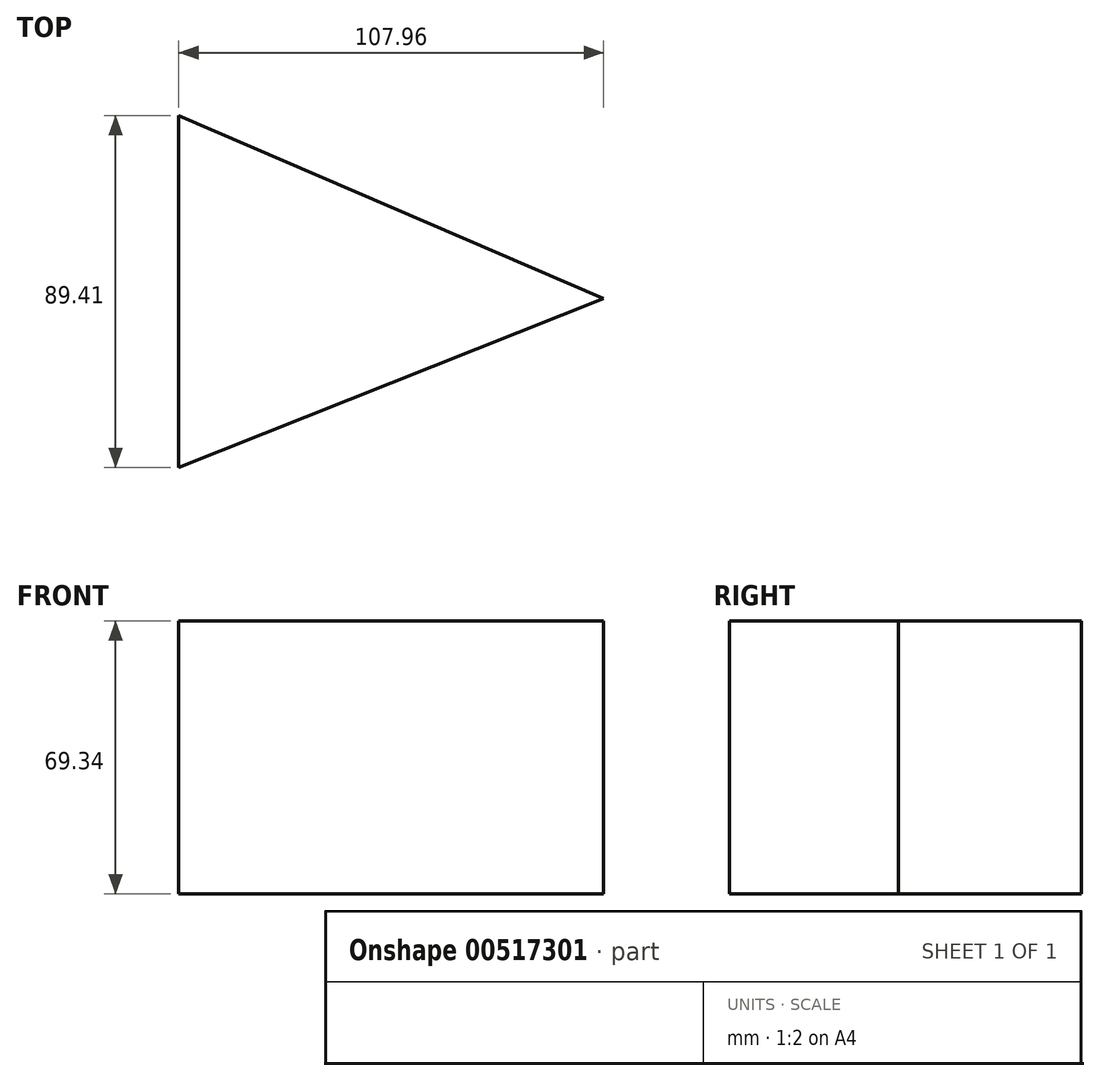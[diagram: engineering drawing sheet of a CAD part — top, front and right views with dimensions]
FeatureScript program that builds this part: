
annotation { "Feature Type Name" : "Feature", "Feature Type Description" : "" }
export const myFeature = defineFeature(function(context is Context, id is Id, definition is map)
    precondition{}
    {
        {
            var Q0;
            Q0=qCreatedBy(makeId("Top.planeOp"),FACE);
            var sketch = newSketch(context, id + "F0", { "sketchPlane" : qUnion([Q0])});
            skLineSegment(sketch, "E0.bottom", {"start": v(-68.92, 46.51) * mm, "end": v(81.46, 46.51) * mm});
            skLineSegment(sketch, "E0.top", {"start": v(-68.92, -42.9) * mm, "end": v(81.46, -42.9) * mm});
            skLineSegment(sketch, "E0.left", {"start": v(-68.92, 46.51) * mm, "end": v(-68.92, -42.9) * mm});
            skLineSegment(sketch, "E0.right", {"start": v(81.46, 46.51) * mm, "end": v(81.46, -42.9) * mm});
            skLineSegment(sketch, "E1", {"start": v(-68.92, -42.9) * mm, "end": v(39.04, 0) * mm});
            skLineSegment(sketch, "E2", {"start": v(39.04, 0) * mm, "end": v(-68.92, 46.51) * mm});
            skSolve(sketch);
        }
        {
            var Q0;
            Q0=makeQuery(id+"F0.imprint","IMPRINT",FACE,{"disambiguationData":[TD([[makeQuery(id+"F0.imprint","IMPRINT",EDGE,{"derivedFrom":sQuery(id+"F0.wireOp",EDGE,"E0.left")}),1.0]])]});
            extrude(context, id + "F1", {"entities" : qUnion([Q0]), "depth" : 69.34 * mm, "offsetDistance" : 25.4 * mm});
        }
    });
